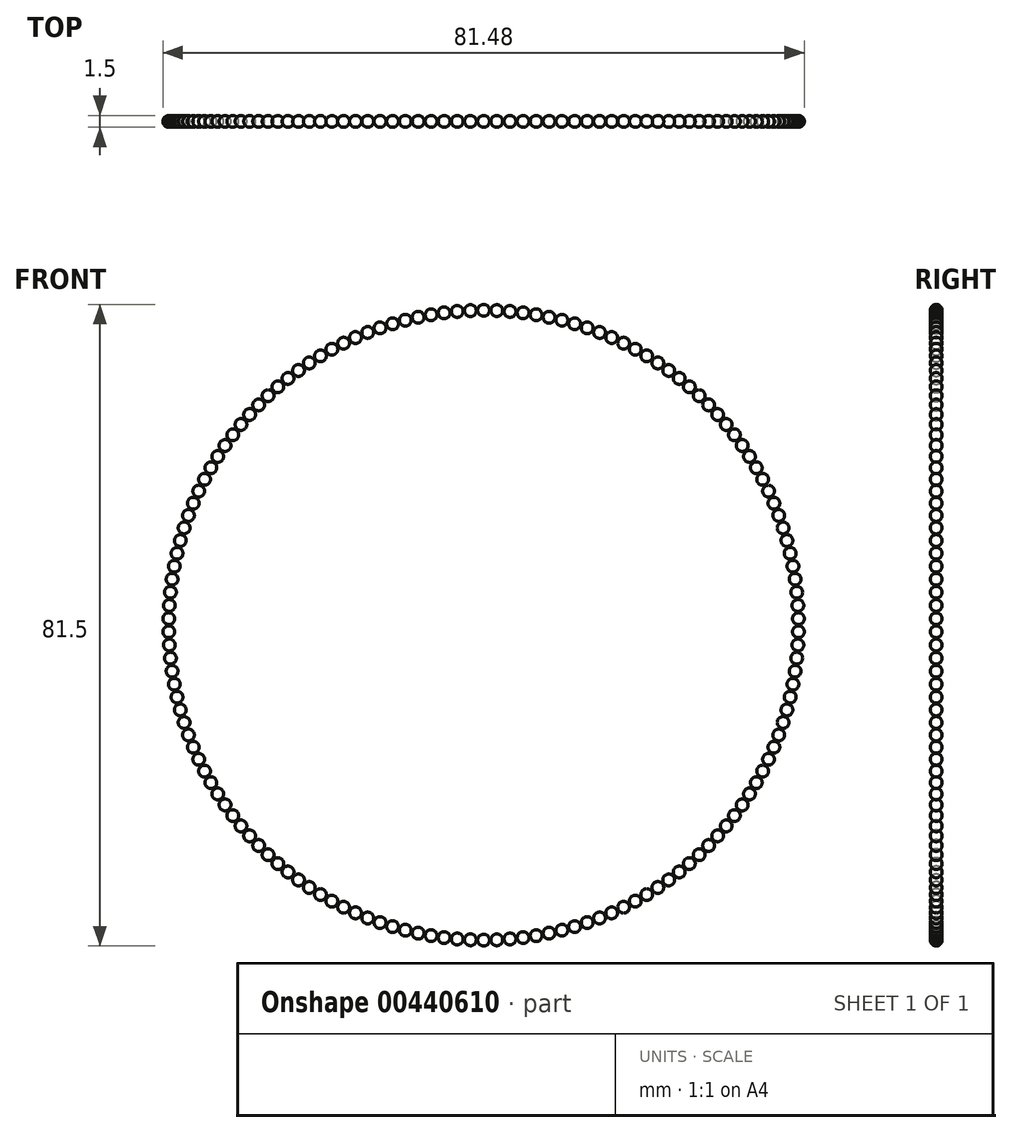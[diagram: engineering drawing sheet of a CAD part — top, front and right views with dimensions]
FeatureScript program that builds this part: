
annotation { "Feature Type Name" : "Feature", "Feature Type Description" : "" }
export const myFeature = defineFeature(function(context is Context, id is Id, definition is map)
    precondition{}
    {
        {
            var Q0;
            Q0=qCreatedBy(makeId("Front.planeOp"),FACE);
            var sketch = newSketch(context, id + "F0", { "sketchPlane" : qUnion([Q0])});
            skCircle(sketch, "E0", {"center": v(0, 0) * mm, "radius": 40 * mm, "construction": true});
            skLineSegment(sketch, "E1", {"start": v(0, 40) * mm, "end": v(0, -40) * mm, "construction": true});
            skLineSegment(sketch, "E2", {"start": v(0, -40) * mm, "end": v(-40, 0) * mm, "construction": true});
            skLineSegment(sketch, "E3", {"start": v(-40, 0) * mm, "end": v(40, 0) * mm, "construction": true});
            skLineSegment(sketch, "E4", {"start": v(40, 0) * mm, "end": v(0, 40) * mm, "construction": true});
            skLineSegment(sketch, "E5", {"start": v(-40, 0) * mm, "end": v(0, 40) * mm, "construction": true});
            skLineSegment(sketch, "E6", {"start": v(40, 0) * mm, "end": v(0, -40) * mm, "construction": true});
            skLineSegment(sketch, "E7", {"start": v(-28.28, 28.28) * mm, "end": v(28.28, -28.28) * mm, "construction": true});
            skLineSegment(sketch, "E8", {"start": v(34.64, -20) * mm, "end": v(-34.64, -20) * mm, "construction": true});
            skLineSegment(sketch, "E9", {"start": v(-28.28, -28.28) * mm, "end": v(28.28, 28.28) * mm, "construction": true});
            skLineSegment(sketch, "E10", {"start": v(34.64, 20) * mm, "end": v(-34.64, 20) * mm, "construction": true});
            skLineSegment(sketch, "E11", {"start": v(-20, 34.64) * mm, "end": v(-20, -34.64) * mm, "construction": true});
            skLineSegment(sketch, "E12", {"start": v(20, -34.64) * mm, "end": v(20, 34.64) * mm, "construction": true});
            skPoint(sketch, "E13.orphan", {"position": v(-20, 20) * mm});
            skPoint(sketch, "E14.orphan", {"position": v(20, 20) * mm});
            skPoint(sketch, "E15.orphan", {"position": v(20, -20) * mm});
            skPoint(sketch, "E16.orphan", {"position": v(-20, -20) * mm});
            skSolve(sketch);
        }
        {
            var Q0;
            Q0=qCreatedBy(makeId("Front.planeOp"),FACE);
            var sketch = newSketch(context, id + "F1", { "sketchPlane" : qUnion([Q0])});
            skLineSegment(sketch, "E17", {"start": v(0, 39.25) * mm, "end": v(0, 40.75) * mm});
            skArc(sketch, "E18", {"start": v(0, 39.25) * mm, "mid": v(0.75, 40) * mm, "end": v(0, 40.75) * mm});
            skSolve(sketch);
        }
        {
            var Q0;
            Q0=makeQuery(id+"F1.imprint","IMPRINT",FACE,{"disambiguationData":[TD([[makeQuery(id+"F1.imprint","IMPRINT",EDGE,{"derivedFrom":sQuery(id+"F1.wireOp",EDGE,"E17")}),-1.0]])]});
            var Q1;
            Q1=sQuery(id+"F1.wireOp",EDGE,"E17");
            revolve(context, id + "F2", {"entities" : qUnion([Q0]), "axis" : qUnion([Q1]), "revolveType" : RevolveType.FULL});
        }
        {
            var Q0;
            Q0=makeQuery(id+"F2.opRevolve","SWEPT_BODY",BODY,{"disambiguationData":[OSD([sQuery(id+"F1.wireOp",EDGE,"E17"),sQuery(id+"F1.wireOp",EDGE,"E18")])]});
            var Q1;
            Q1=sQuery(id+"F0.wireOp",EDGE,"E0");
            circularPattern(context, id + "F3", {"entities" : qUnion([Q0]), "axis" : qUnion([Q1]), "angle" : 360 * degree, "instanceCount" : 150, "equalSpace" : true, "isCentered" : true});
        }
    });
